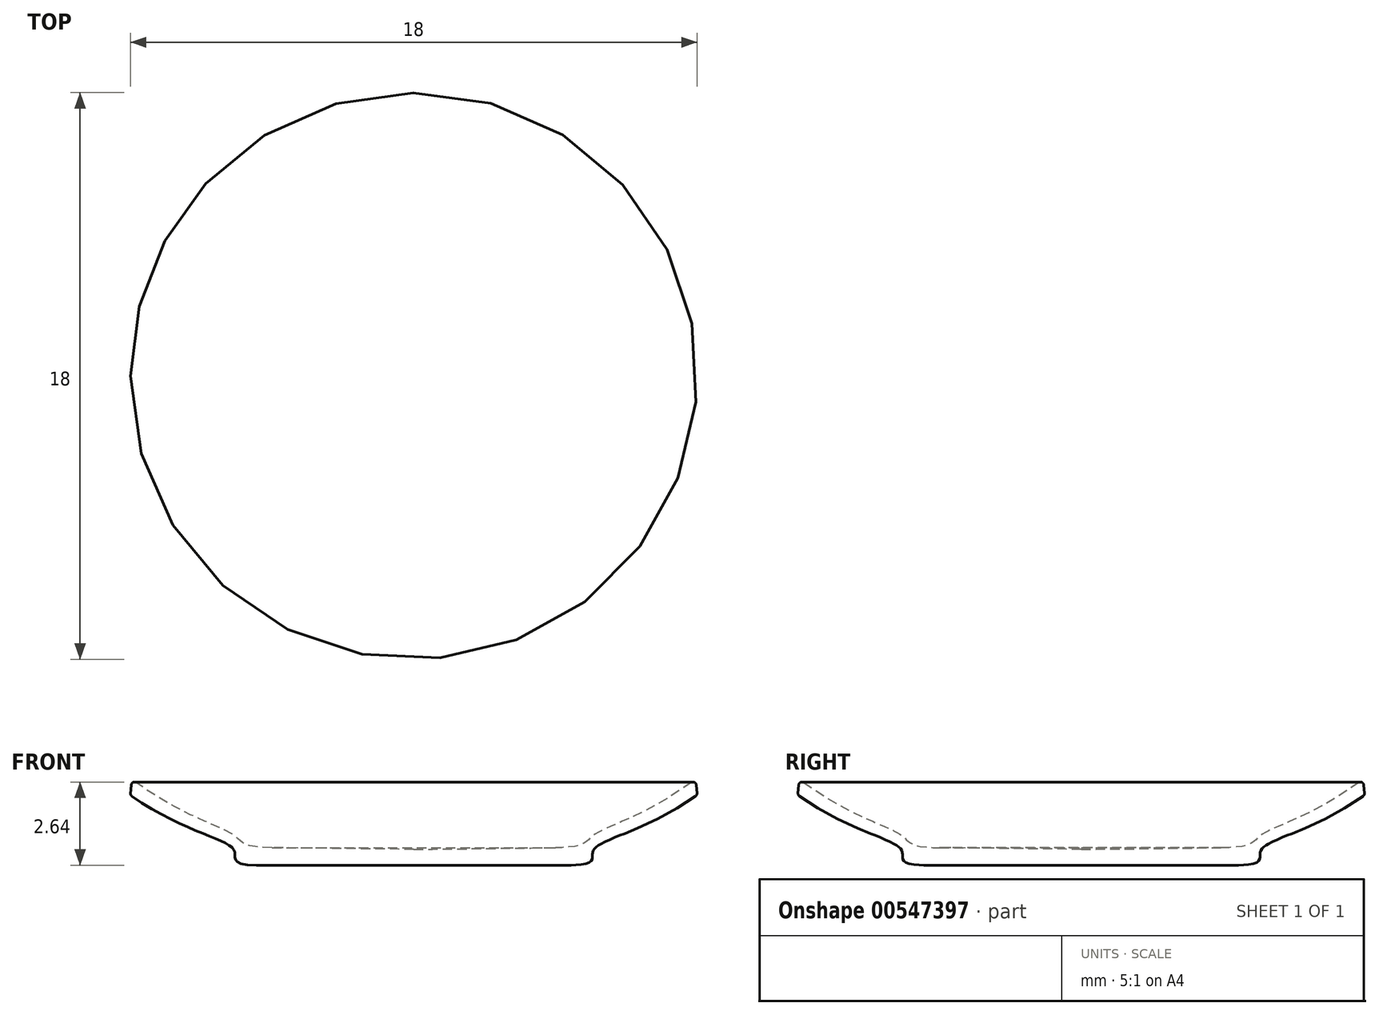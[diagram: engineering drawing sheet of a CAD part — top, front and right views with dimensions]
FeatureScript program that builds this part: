
annotation { "Feature Type Name" : "Feature", "Feature Type Description" : "" }
export const myFeature = defineFeature(function(context is Context, id is Id, definition is map)
    precondition{}
    {
        {
            var Q0;
            Q0=qCreatedBy(makeId("Front.planeOp"),FACE);
            var sketch = newSketch(context, id + "F0", { "sketchPlane" : qUnion([Q0])});
            skLineSegment(sketch, "E0", {"start": v(0, 0) * mm, "end": v(5, 0) * mm});
            skFitSpline(sketch, "E1", {"points": [v(5, 0) * mm, v(5.7, 0.44) * mm, v(9, 2.23) * mm], "startDerivative": vector(8.09, 0) * mm, "endDerivative": vector(7.48, 5.38) * mm});
            skLineSegment(sketch, "E2", {"start": v(0, 0) * mm, "end": v(0, 0.5) * mm});
            skLineSegment(sketch, "E3", {"start": v(0, 0.5) * mm, "end": v(4.5, 0.56) * mm});
            skFitSpline(sketch, "E4", {"points": [v(4.5, 0.56) * mm, v(5.7, 0.94) * mm, v(8.95, 2.73) * mm], "startDerivative": vector(8.07, 0) * mm, "endDerivative": vector(7.84, 5.79) * mm});
            skLineSegment(sketch, "E5", {"start": v(8.95, 2.73) * mm, "end": v(9, 2.23) * mm});
            skLineSegment(sketch, "E6", {"start": v(5.86, 2.05) * mm, "end": v(5.86, -1.4) * mm, "construction": true});
            skLineSegment(sketch, "E7", {"start": v(7.3, 2.66) * mm, "end": v(7.3, -1.31) * mm, "construction": true});
            skSolve(sketch);
        }
        {
            var Q0;
            Q0=makeQuery(id+"F0.imprint","IMPRINT",FACE,{"disambiguationData":[TD([[makeQuery(id+"F0.imprint","IMPRINT",EDGE,{"derivedFrom":sQuery(id+"F0.wireOp",EDGE,"E0")}),1.0]])]});
            var Q1;
            Q1=sQuery(id+"F0.wireOp",EDGE,"E2");
            revolve(context, id + "F1", {"entities" : qUnion([Q0]), "axis" : qUnion([Q1]), "revolveType" : RevolveType.FULL});
        }
        {
            var Q0;
            Q0=makeQuery(id+"F1.opRevolve","SWEPT_EDGE",EDGE,{"disambiguationData":[OSD([sQuery(id+"F0.wireOp",EDGE,"E4"),sQuery(id+"F0.wireOp",EDGE,"E5")])]});
            var Q1;
            Q1=makeQuery(id+"F1.opRevolve","SWEPT_EDGE",EDGE,{"disambiguationData":[OSD([sQuery(id+"F0.wireOp",EDGE,"E1"),sQuery(id+"F0.wireOp",EDGE,"E5")])]});
            var Q2;
            Q2=makeQuery(id+"F1.opRevolve","SWEPT_EDGE",EDGE,{"disambiguationData":[OSD([sQuery(id+"F0.wireOp",EDGE,"E3"),sQuery(id+"F0.wireOp",EDGE,"E4")])]});
            fillet(context, id + "F2", {"entities" : qUnion([Q0, Q1, Q2]), "radius" : 0.1 * mm, "tangentPropagation" : true, "allowEdgeOverflow" : false});
        }
    });
